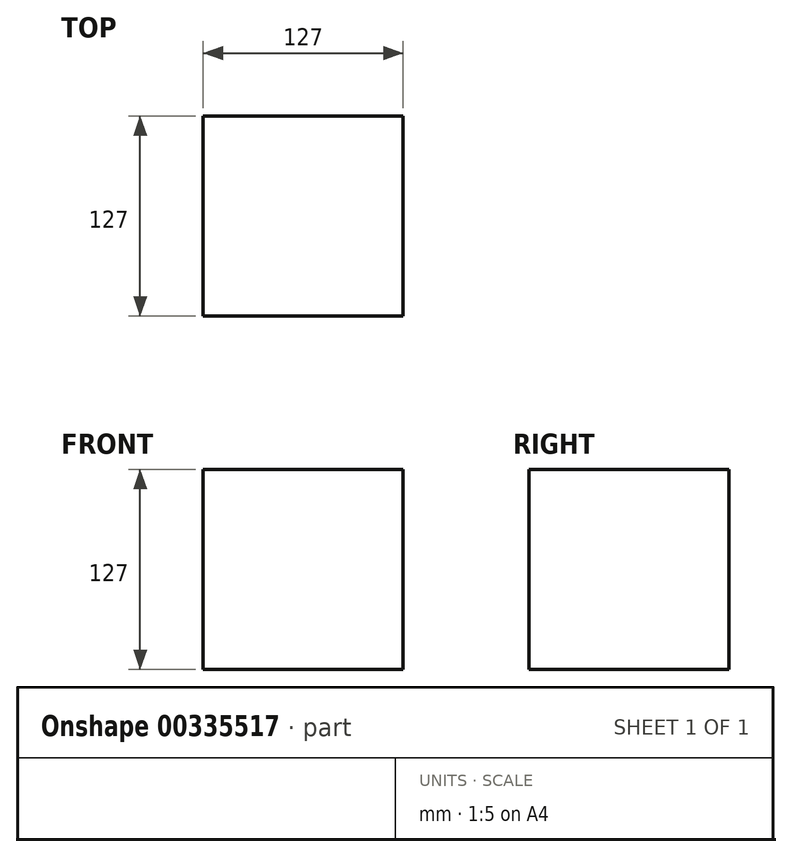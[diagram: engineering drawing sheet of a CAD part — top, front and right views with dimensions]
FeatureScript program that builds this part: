
annotation { "Feature Type Name" : "Feature", "Feature Type Description" : "" }
export const myFeature = defineFeature(function(context is Context, id is Id, definition is map)
    precondition{}
    {
        {
            var Q0;
            Q0=qCreatedBy(makeId("Top.planeOp"),FACE);
            var sketch = newSketch(context, id + "F0", { "sketchPlane" : qUnion([Q0])});
            skLineSegment(sketch, "E0.bottom", {"start": v(-30.51, 56.18) * mm, "end": v(96.49, 56.18) * mm});
            skLineSegment(sketch, "E0.top", {"start": v(-30.51, -70.82) * mm, "end": v(96.49, -70.82) * mm});
            skLineSegment(sketch, "E0.left", {"start": v(-30.51, 56.18) * mm, "end": v(-30.51, -70.82) * mm});
            skLineSegment(sketch, "E0.right", {"start": v(96.49, 56.18) * mm, "end": v(96.49, -70.82) * mm});
            skPoint(sketch, "E0.middle", {"position": v(32.99, -7.32) * mm});
            skSolve(sketch);
        }
        {
            var Q0;
            Q0 = qSketchRegion(id + "F0", true);
            extrude(context, id + "F1", {"entities" : qUnion([Q0]), "depth" : 127 * mm});
        }
    });
